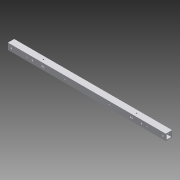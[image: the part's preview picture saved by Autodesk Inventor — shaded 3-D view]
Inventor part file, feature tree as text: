
AUTODESK INVENTOR PART (.ipt)
format: ipt  version: 2015 SP1 (Build 190203100, 203)  size: 170,496 bytes
history: native  units: in
note: dims shown in document units (in); Inventor stores cm internally (conversion verified against a paired STEP export)
features: sketch x6, hole x4, extrude x2
ambient origin geometry x8: Origin, YZ Plane, XZ Plane, XY Plane, X Axis, Y Axis, Z Axis, Center Point
bodies: Solid1 (feature_tree)
feature tree (12):
  extrude  "Extrusion1"  Depth=1.0in
  hole  "Hole1"  [1 undecoded]
  hole  "Hole2"  [1 undecoded]
  hole  "Hole3"  [1 undecoded]
  extrude  "Extrusion2"  Depth=0.5in
  hole  "Hole5"  [1 undecoded]
  sketch  "Sketch1"  dims[d0=1.0in d1=1.0in]
  sketch  "Sketch2"  dims[d2=0.75in d3=0.75in]
  sketch  "Sketch3"  dims[d4=0.125in d5=0.125in]
  sketch  "Sketch4"  dims[d6=25.0in d7=0.0in d8=3.875in]
  sketch  "Sketch6"  dims[d9=1.5in d10=0.5in]
  sketch  "Sketch7"  dims[d11=0.5in d12=0.5in d13=3.875in d14=1.5in d15=0.5in d16=0.25in d17=0.75in d18=0.375in d19=0.25in d20=0.5635in d21=1.0in d22=0.8108in d23=0.5in d24=0.5in d25=0.5in d26=0.5in d27=0.25in d28=0.75in d29=0.375in d30=0.25in d31=0.5635in d32=1.0in d33=0.8108in d34=0.5in d35=0.5in d36=0.5in d37=0.5in d38=3.0in d39=9.0in d40=9.0in d41=3.0in d42=0.1875in d43=0.75in d44=0.375in d45=0.25in d46=0.5635in d47=1.0in d48=0.8108in d61=0.25in d62=0.25in d63=0.25in d64=0.5in d65=0.25in d66=0.5in d67=1.0in d68=0.0in d69=0.5in d70=5.125in d71=0.5in d74=0.1875in d75=0.75in d76=0.375in d77=0.25in d78=0.5635in d79=1.0in d80=0.8108in d81=14.75in]
note: 4 required parameter values undecoded (feature->parameter linkage not recoverable at this tier; creation-order binding heuristic only, values carry confidence <= 0.55)
